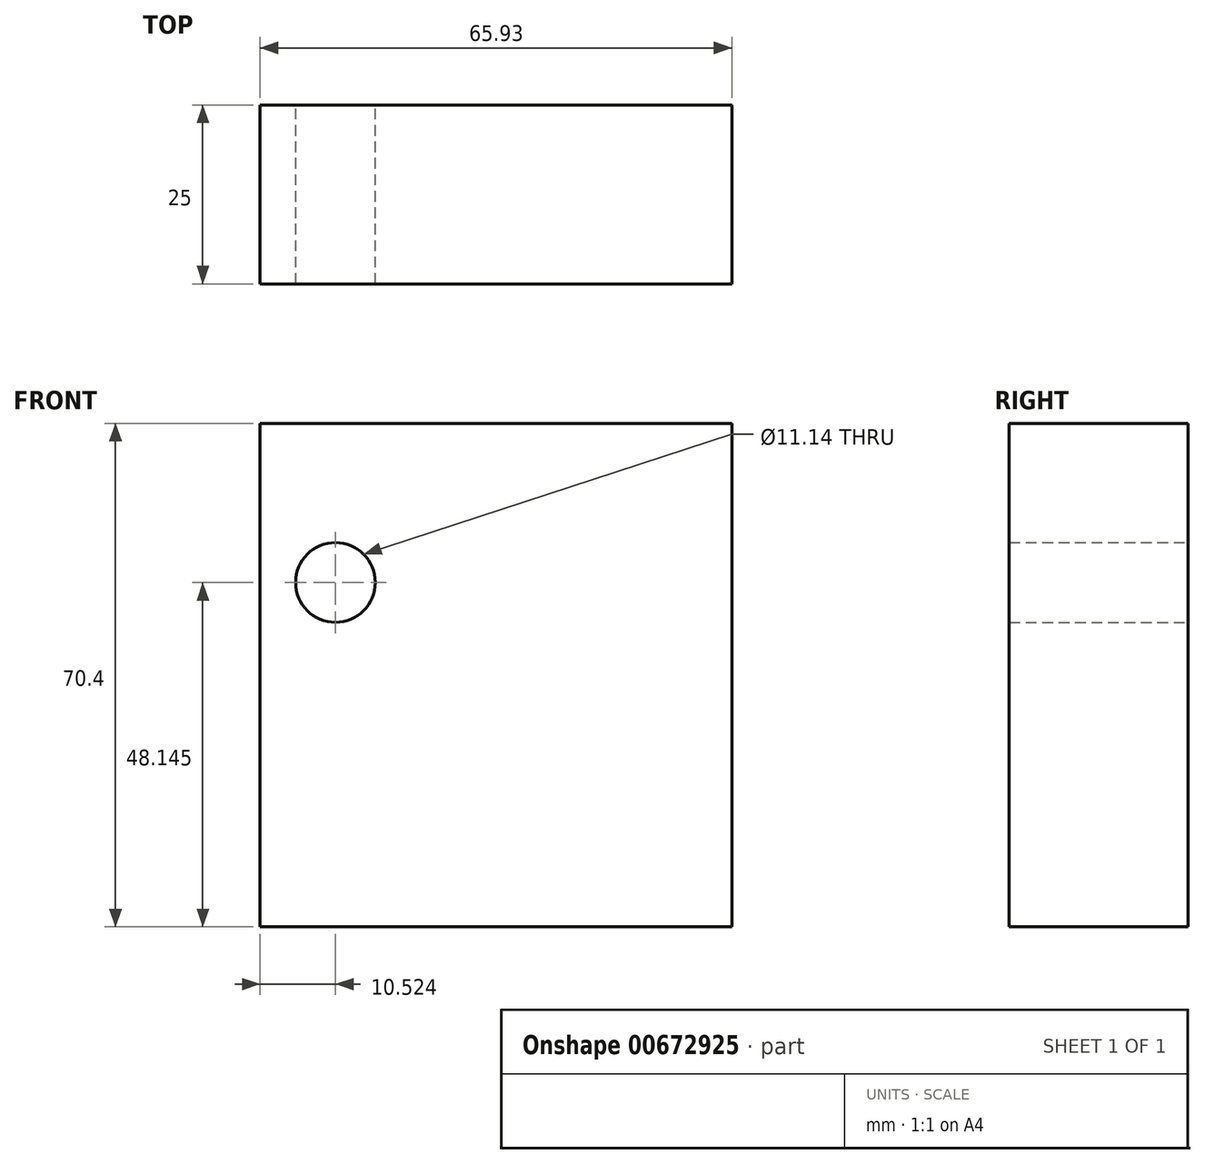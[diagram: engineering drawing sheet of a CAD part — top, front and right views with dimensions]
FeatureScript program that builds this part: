
annotation { "Feature Type Name" : "Feature", "Feature Type Description" : "" }
export const myFeature = defineFeature(function(context is Context, id is Id, definition is map)
    precondition{}
    {
        {
            var Q0;
            Q0=qCreatedBy(makeId("Front.planeOp"),FACE);
            var sketch = newSketch(context, id + "F0", { "sketchPlane" : qUnion([Q0])});
            skLineSegment(sketch, "E0.bottom", {"start": v(0, 0) * mm, "end": v(65.93, 0) * mm});
            skLineSegment(sketch, "E0.top", {"start": v(0, 70.4) * mm, "end": v(65.93, 70.4) * mm});
            skLineSegment(sketch, "E0.left", {"start": v(0, 0) * mm, "end": v(0, 70.4) * mm});
            skLineSegment(sketch, "E0.right", {"start": v(65.93, 0) * mm, "end": v(65.93, 70.4) * mm});
            skCircle(sketch, "E1", {"center": v(10.52, 48.15) * mm, "radius": 5.57 * mm});
            skSolve(sketch);
        }
        {
            var Q0;
            Q0 = qSketchRegion(id + "F0", true);
            extrude(context, id + "F1", {"entities" : qUnion([Q0]), "depth" : 25 * mm, "offsetDistance" : 25 * mm});
        }
    });
